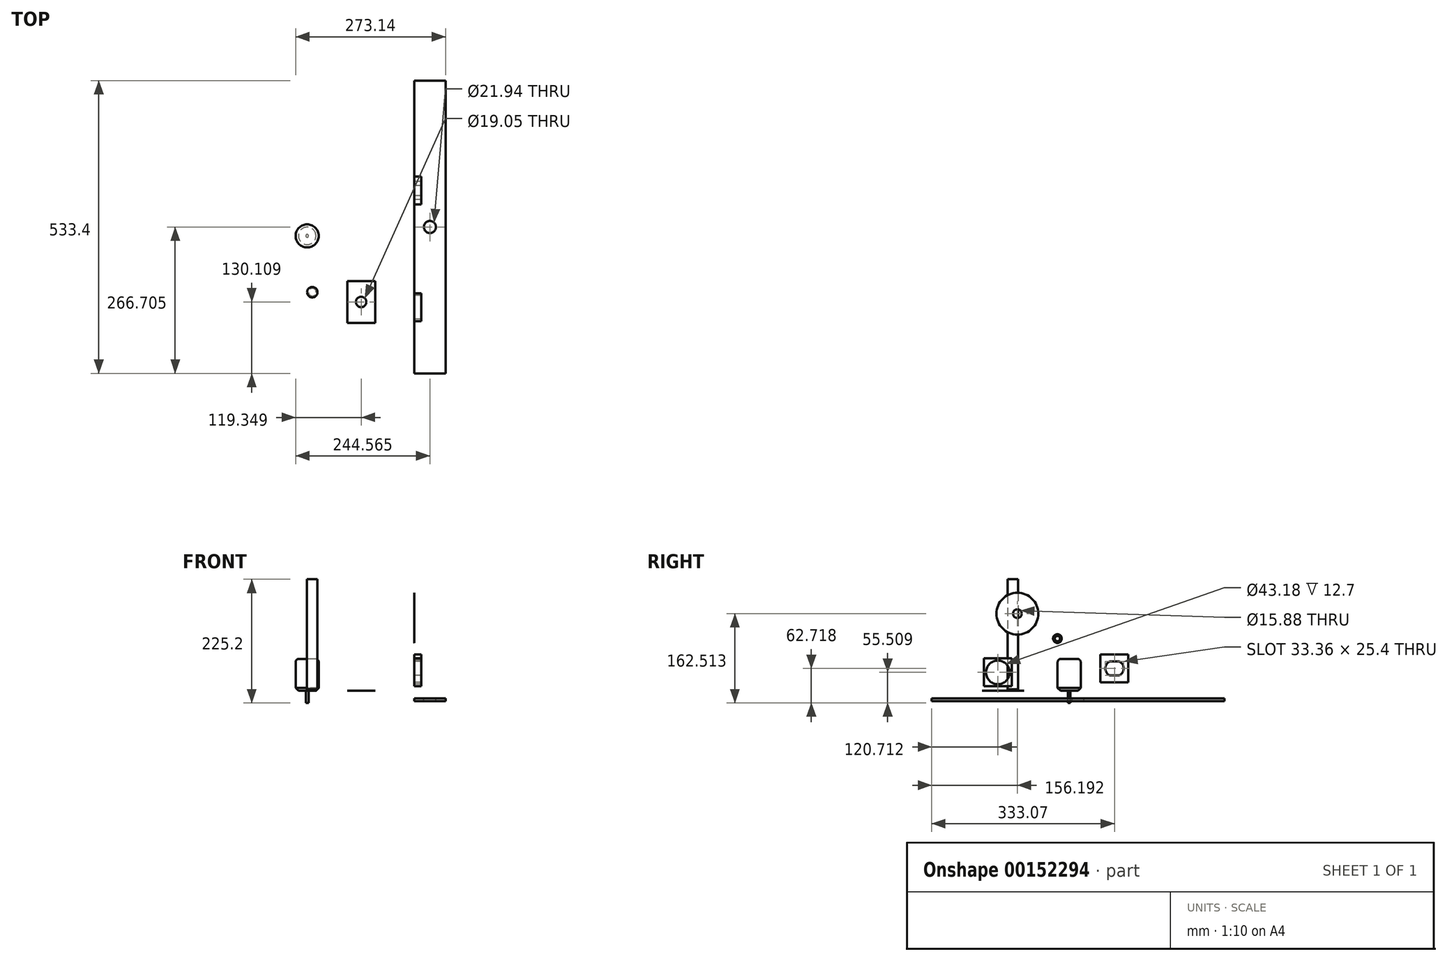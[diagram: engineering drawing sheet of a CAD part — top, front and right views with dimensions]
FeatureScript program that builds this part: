
annotation { "Feature Type Name" : "Feature", "Feature Type Description" : "" }
export const myFeature = defineFeature(function(context is Context, id is Id, definition is map)
    precondition{}
    {
        {
            var Q0;
            Q0=qCreatedBy(makeId("Right.planeOp"),FACE);
            var sketch = newSketch(context, id + "F0", { "sketchPlane" : qUnion([Q0])});
            skLineSegment(sketch, "E0.bottom", {"start": v(-201.34, -13.9) * mm, "end": v(332.06, -13.9) * mm});
            skLineSegment(sketch, "E0.top", {"start": v(-201.34, -18.97) * mm, "end": v(332.06, -18.97) * mm});
            skLineSegment(sketch, "E0.left", {"start": v(-201.34, -13.9) * mm, "end": v(-201.34, -18.97) * mm});
            skLineSegment(sketch, "E0.right", {"start": v(332.06, -13.9) * mm, "end": v(332.06, -18.97) * mm});
            skSolve(sketch);
        }
        {
            var Q0;
            Q0 = qSketchRegion(id + "F0", true);
            extrude(context, id + "F1", {"entities" : qUnion([Q0]), "depth" : 57.15 * mm});
        }
        {
            var Q0;
            Q0=qCreatedBy(makeId("Top.planeOp"),FACE);
            var sketch = newSketch(context, id + "F2", { "sketchPlane" : qUnion([Q0])});
            skCircle(sketch, "E1", {"center": v(-105.34, -53.49) * mm, "radius": 25 * mm});
            skSolve(sketch);
        }
        {
            var Q0;
            Q0 = qSketchRegion(id + "F2", true);
            extrude(context, id + "F3", {"entities" : qUnion([Q0]), "depth" : 55 * mm});
        }
        {
            var Q0;
            Q0=makeQuery(id+"F3.opExtrude","CAP_EDGE",EDGE,{"disambiguationData":[OSD([sQuery(id+"F2.wireOp",EDGE,"E1")])],"isStart":false});
            chamfer(context, id + "F4", {"entities" : qUnion([Q0]), "width" : 5.08 * mm, "tangentPropagation" : true});
        }
        {
            var Q0;
            Q0=makeQuery(id+"F3.opExtrude","CAP_FACE",FACE,{"disambiguationData":[OSD([sQuery(id+"F2.wireOp",EDGE,"E1")])],"isStart":true});
            var sketch = newSketch(context, id + "F5", { "sketchPlane" : qUnion([Q0])});
            skCircle(sketch, "E2", {"center": v(-105.34, 53.49) * mm, "radius": 3 * mm});
            skSolve(sketch);
        }
        {
            var Q0;
            Q0 = qSketchRegion(id + "F5", true);
            extrude(context, id + "F6", {"entities" : qUnion([Q0]), "operationType" : NewBodyOperationType.ADD, "depth" : 19.05 * mm});
        }
        {
            var Q0;
            Q0=qCreatedBy(makeId("Right.planeOp"),FACE);
            var sketch = newSketch(context, id + "F7", { "sketchPlane" : qUnion([Q0])});
            skCircle(sketch, "E3", {"center": v(27.82, 95.12) * mm, "radius": 7.94 * mm});
            skCircle(sketch, "E4", {"center": v(27.82, 95.12) * mm, "radius": 4.76 * mm});
            skSolve(sketch);
        }
        {
            var Q0;
            Q0 = qSketchRegion(id + "F7", true);
            extrude(context, id + "F8", {"entities" : qUnion([Q0]), "depth" : 7 / 203.2 * mm});
        }
        {
            var Q0;
            Q0=qCreatedBy(makeId("Right.planeOp"),FACE);
            var sketch = newSketch(context, id + "F9", { "sketchPlane" : qUnion([Q0])});
            skCircle(sketch, "E5", {"center": v(-45.15, 140.51) * mm, "radius": 38.1 * mm});
            skCircle(sketch, "E6", {"center": v(-45.15, 140.51) * mm, "radius": 7.94 * mm});
            skSolve(sketch);
        }
        {
            var Q0;
            Q0 = qSketchRegion(id + "F9", true);
            extrude(context, id + "F10", {"entities" : qUnion([Q0]), "depth" : 7 / 203.2 * mm});
        }
        {
            var Q0;
            Q0=makeQuery(id+"F1.opExtrude","SWEPT_FACE",FACE,{"disambiguationData":[OSD([sQuery(id+"F0.wireOp",EDGE,"E0.bottom")])]});
            var sketch = newSketch(context, id + "F11", { "sketchPlane" : qUnion([Q0])});
            skCircle(sketch, "E7", {"center": v(28.58, 65.36) * mm, "radius": 10.97 * mm});
            skPoint(sketch, "E7.centerSnap0", {"position": v(57.15, 65.36) * mm});
            skPoint(sketch, "E7.centerSnap1", {"position": v(28.58, 332.06) * mm});
            skSolve(sketch);
        }
        {
            var Q0;
            Q0 = qSketchRegion(id + "F11", true);
            extrude(context, id + "F12", {"entities" : qUnion([Q0]), "operationType" : NewBodyOperationType.REMOVE, "oppositeDirection" : true, "depth" : 25.4 * mm});
        }
        {
            var Q0;
            Q0=makeQuery(id+"F3.opExtrude","SWEPT_BODY",BODY,{"disambiguationData":[OSD([sQuery(id+"F2.wireOp",EDGE,"E1")])]});
            deleteBodies(context, id + "F13", {"entities" : qUnion([Q0])});
        }
        {
            var Q0;
            Q0=qCreatedBy(makeId("Top.planeOp"),FACE);
            var sketch = newSketch(context, id + "F14", { "sketchPlane" : qUnion([Q0])});
            skCircle(sketch, "E8", {"center": v(-194.99, 49.2) * mm, "radius": 21 * mm});
            skSolve(sketch);
        }
        {
            var Q0;
            Q0 = qSketchRegion(id + "F14", true);
            extrude(context, id + "F15", {"entities" : qUnion([Q0]), "depth" : 58 * mm});
        }
        {
            var Q0;
            Q0=makeQuery(id+"F15.opExtrude","CAP_EDGE",EDGE,{"disambiguationData":[OSD([sQuery(id+"F14.wireOp",EDGE,"E8")])],"isStart":true});
            chamfer(context, id + "F16", {"entities" : qUnion([Q0]), "width" : 5.08 * mm, "tangentPropagation" : true});
        }
        {
            var Q0;
            Q0=makeQuery(id+"F15.opExtrude","CAP_EDGE",EDGE,{"disambiguationData":[OSD([sQuery(id+"F14.wireOp",EDGE,"E8")])],"isStart":false});
            fillet(context, id + "F17", {"entities" : qUnion([Q0]), "radius" : 5.6 * mm, "tangentPropagation" : true, "allowEdgeOverflow" : false});
        }
        {
            var Q0;
            Q0=makeQuery(id+"F15.opExtrude","CAP_FACE",FACE,{"disambiguationData":[OSD([sQuery(id+"F14.wireOp",EDGE,"E8")])],"isStart":true});
            var sketch = newSketch(context, id + "F18", { "sketchPlane" : qUnion([Q0])});
            skCircle(sketch, "E9", {"center": v(-194.99, -49.2) * mm, "radius": 2.5 * mm});
            skSolve(sketch);
        }
        {
            var Q0;
            Q0 = qSketchRegion(id + "F18", true);
            extrude(context, id + "F19", {"entities" : qUnion([Q0]), "operationType" : NewBodyOperationType.ADD, "depth" : 22 * mm});
        }
        {
            var Q0;
            Q0=qCreatedBy(makeId("Right.planeOp"),FACE);
            var sketch = newSketch(context, id + "F20", { "sketchPlane" : qUnion([Q0])});
            skLineSegment(sketch, "E10.bottom", {"start": v(-55.23, 8.1) * mm, "end": v(-106.03, 8.1) * mm});
            skLineSegment(sketch, "E10.top", {"start": v(-55.23, 58.9) * mm, "end": v(-106.03, 58.9) * mm});
            skLineSegment(sketch, "E10.left", {"start": v(-55.23, 8.1) * mm, "end": v(-55.23, 58.9) * mm});
            skLineSegment(sketch, "E10.right", {"start": v(-106.03, 8.1) * mm, "end": v(-106.03, 58.9) * mm});
            skCircle(sketch, "E11", {"center": v(-80.63, 33.5) * mm, "radius": 21.59 * mm});
            skPoint(sketch, "E11.centerSnap0", {"position": v(-80.63, 58.9) * mm});
            skPoint(sketch, "E11.centerSnap1", {"position": v(-106.03, 33.5) * mm});
            skSolve(sketch);
        }
        {
            var Q0;
            Q0 = qSketchRegion(id + "F20", true);
            extrude(context, id + "F21", {"entities" : qUnion([Q0]), "depth" : 12.7 * mm});
        }
        {
            var Q0;
            Q0=qCreatedBy(makeId("Right.planeOp"),FACE);
            var sketch = newSketch(context, id + "F22", { "sketchPlane" : qUnion([Q0])});
            skLineSegment(sketch, "E12.bottom", {"start": v(106.23, 15.32) * mm, "end": v(157.03, 15.32) * mm});
            skLineSegment(sketch, "E12.top", {"start": v(106.23, 66.12) * mm, "end": v(157.03, 66.12) * mm});
            skLineSegment(sketch, "E12.left", {"start": v(106.23, 15.32) * mm, "end": v(106.23, 66.12) * mm});
            skLineSegment(sketch, "E12.right", {"start": v(157.03, 15.32) * mm, "end": v(157.03, 66.12) * mm});
            skLineSegment(sketch, "E13.bottom", {"start": v(140.62, 53.42) * mm, "end": v(122.64, 53.42) * mm});
            skLineSegment(sketch, "E13.top", {"start": v(140.62, 28.02) * mm, "end": v(122.64, 28.02) * mm});
            skLineSegment(sketch, "E13.left", {"start": v(140.62, 53.42) * mm, "end": v(140.62, 28.02) * mm});
            skLineSegment(sketch, "E13.right", {"start": v(122.64, 53.42) * mm, "end": v(122.64, 28.02) * mm});
            skPoint(sketch, "E13.middle", {"position": v(131.63, 40.72) * mm});
            skPoint(sketch, "E13.middle.positionSnap0", {"position": v(131.63, 66.12) * mm});
            skPoint(sketch, "E13.middle.positionSnap1", {"position": v(157.03, 40.72) * mm});
            skPoint(sketch, "E13.centerSnap0", {"position": v(131.63, 66.12) * mm});
            skPoint(sketch, "E13.centerSnap1", {"position": v(157.03, 40.72) * mm});
            skArc(sketch, "E14", {"start": v(122.64, 53.42) * mm, "mid": v(115.05, 40.72) * mm, "end": v(122.64, 28.02) * mm});
            skArc(sketch, "E15", {"start": v(140.62, 28.02) * mm, "mid": v(148.41, 40.72) * mm, "end": v(140.62, 53.42) * mm});
            skSolve(sketch);
        }
        {
            var Q0;
            Q0 = qSketchRegion(id + "F22", true);
            extrude(context, id + "F23", {"entities" : qUnion([Q0]), "depth" : 12.7 * mm});
        }
        {
            var Q0;
            Q0=qCreatedBy(makeId("Top.planeOp"),FACE);
            var sketch = newSketch(context, id + "F24", { "sketchPlane" : qUnion([Q0])});
            skLineSegment(sketch, "E16.bottom", {"start": v(-71.24, -33.13) * mm, "end": v(-122.04, -33.13) * mm});
            skLineSegment(sketch, "E16.top", {"start": v(-71.24, -109.33) * mm, "end": v(-122.04, -109.33) * mm});
            skLineSegment(sketch, "E16.left", {"start": v(-71.24, -33.13) * mm, "end": v(-71.24, -109.33) * mm});
            skLineSegment(sketch, "E16.right", {"start": v(-122.04, -33.13) * mm, "end": v(-122.04, -109.33) * mm});
            skPoint(sketch, "E16.middle", {"position": v(-96.64, -71.23) * mm});
            skCircle(sketch, "E17", {"center": v(-96.64, -71.23) * mm, "radius": 9.53 * mm});
            skSolve(sketch);
        }
        {
            var Q0;
            Q0 = qSketchRegion(id + "F24", true);
            extrude(context, id + "F25", {"entities" : qUnion([Q0]), "depth" : 5 / 406.4 * mm});
        }
        {
            var Q0;
            Q0=qCreatedBy(makeId("Top.planeOp"),FACE);
            var sketch = newSketch(context, id + "F26", { "sketchPlane" : qUnion([Q0])});
            skCircle(sketch, "E18", {"center": v(-185.58, -53.4) * mm, "radius": 9.53 * mm});
            skSolve(sketch);
        }
        {
            var Q0;
            Q0 = qSketchRegion(id + "F26", true);
            extrude(context, id + "F27", {"entities" : qUnion([Q0]), "depth" : 203.2 * mm});
        }
        {
            var Q0;
            Q0=makeQuery(id+"F27.opExtrude","CAP_EDGE",EDGE,{"disambiguationData":[OSD([sQuery(id+"F26.wireOp",EDGE,"E18")])],"isStart":true});
            chamfer(context, id + "F28", {"entities" : qUnion([Q0]), "width" : 2.54 * mm, "tangentPropagation" : true});
        }
    });
